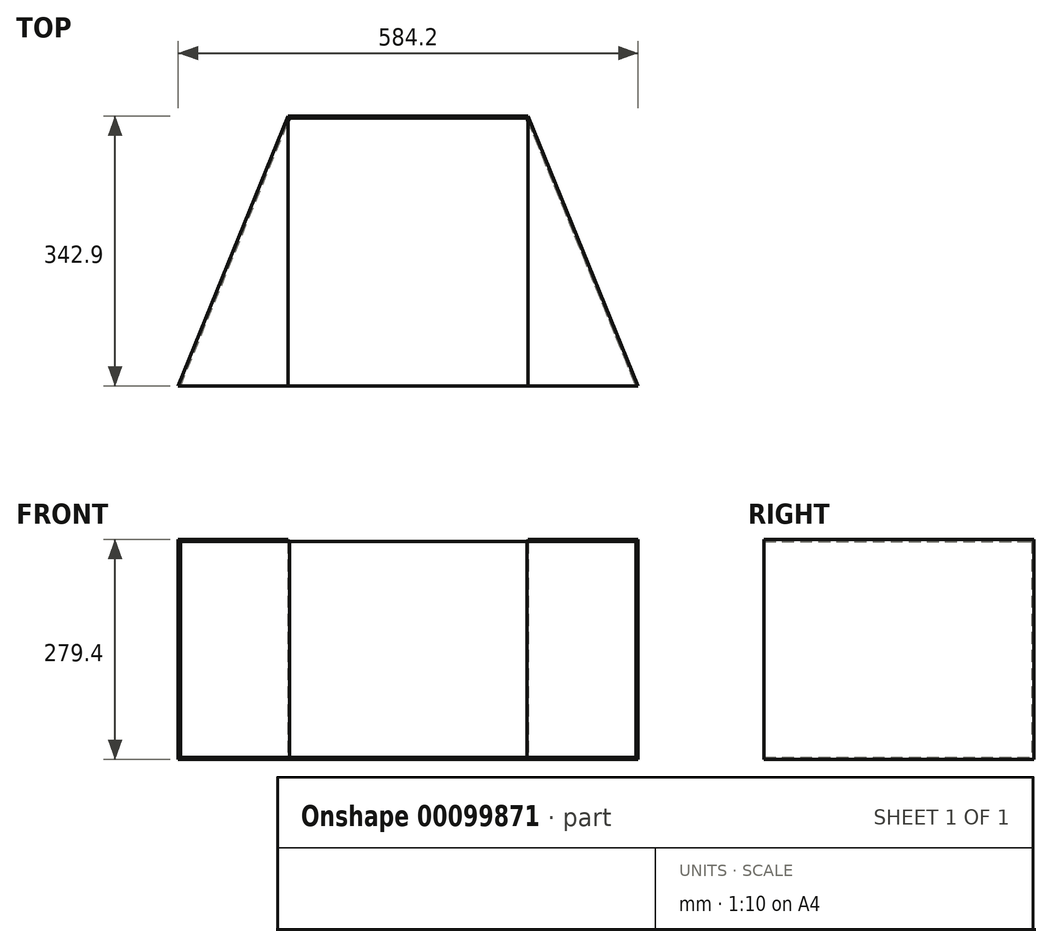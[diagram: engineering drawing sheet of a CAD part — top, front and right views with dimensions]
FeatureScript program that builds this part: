
annotation { "Feature Type Name" : "Feature", "Feature Type Description" : "" }
export const myFeature = defineFeature(function(context is Context, id is Id, definition is map)
    precondition{}
    {
        {
            var Q0;
            Q0=qCreatedBy(makeId("Top.planeOp"),FACE);
            var sketch = newSketch(context, id + "F0", { "sketchPlane" : qUnion([Q0])});
            skLineSegment(sketch, "E0", {"start": v(-292.1, 0) * mm, "end": v(-152.4, 342.9) * mm});
            skLineSegment(sketch, "E1", {"start": v(-152.4, 342.9) * mm, "end": v(152.4, 342.9) * mm});
            skLineSegment(sketch, "E2", {"start": v(152.4, 342.9) * mm, "end": v(292.1, 0) * mm});
            skLineSegment(sketch, "E3", {"start": v(292.1, 0) * mm, "end": v(-292.1, 0) * mm});
            skSolve(sketch);
        }
        {
            var Q0;
            Q0 = qSketchRegion(id + "F0", true);
            extrude(context, id + "F1", {"entities" : qUnion([Q0]), "endBound" : BoundingType.SYMMETRIC, "depth" : 279.4 * mm});
        }
        {
            var Q0;
            Q0=makeQuery(id+"F1.opExtrude","SWEPT_FACE",FACE,{"disambiguationData":[OSD([sQuery(id+"F0.wireOp",EDGE,"E3")])]});
            shell(context, id + "F2", {"entities" : qUnion([Q0]), "thickness" : 2.54 * mm});
        }
        {
            var Q0;
            Q0=makeQuery(id+"F1.opExtrude","CAP_FACE",FACE,{"disambiguationData":[OSD([sQuery(id+"F0.wireOp",EDGE,"E0"),sQuery(id+"F0.wireOp",EDGE,"E1"),sQuery(id+"F0.wireOp",EDGE,"E2"),sQuery(id+"F0.wireOp",EDGE,"E3")])],"isStart":false});
            var sketch = newSketch(context, id + "F3", { "sketchPlane" : qUnion([Q0])});
            skLineSegment(sketch, "E4.bottom", {"start": v(-152.4, 342.9) * mm, "end": v(152.4, 342.9) * mm});
            skLineSegment(sketch, "E4.top", {"start": v(-152.4, 0) * mm, "end": v(152.4, 0) * mm});
            skLineSegment(sketch, "E4.left", {"start": v(-152.4, 342.9) * mm, "end": v(-152.4, 0) * mm});
            skLineSegment(sketch, "E4.right", {"start": v(152.4, 342.9) * mm, "end": v(152.4, 0) * mm});
            skSolve(sketch);
        }
        {
            var Q0;
            Q0 = qSketchRegion(id + "F3", true);
            var Q1;
            {var subQ0=sQuery(id+"F0.wireOp",EDGE,"E3");var subQ1=sQuery(id+"F0.wireOp",EDGE,"E2");var subQ2=sQuery(id+"F0.wireOp",EDGE,"E1");var subQ3=sQuery(id+"F0.wireOp",EDGE,"E0");Q1=makeQuery(id+"F2.opShell","OFFSET_FACE",FACE,{"disambiguationData":[OSD([subQ3,subQ2,subQ1,subQ0]),TDD([makeQuery(id+"F1.opExtrude","CAP_FACE",FACE,{"disambiguationData":[OSD([subQ3,subQ2,subQ1,subQ0])],"isStart":false})])]});}
            extrude(context, id + "F4", {"entities" : qUnion([Q0]), "operationType" : NewBodyOperationType.REMOVE, "endBound" : BoundingType.UP_TO_SURFACE, "oppositeDirection" : true, "endBoundEntityFace" : qUnion([Q1]), "depth" : 25.4 * mm});
        }
    });
